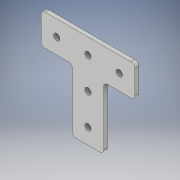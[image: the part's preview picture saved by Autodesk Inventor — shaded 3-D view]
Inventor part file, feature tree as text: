
AUTODESK INVENTOR PART (.ipt)
format: ipt  version: 2018 (Build 220112000, 112)  size: 137,728 bytes
history: native  units: in
note: dims shown in document units (in); Inventor stores cm internally (conversion verified against a paired STEP export)
features: extrude x2, sketch x2, fillet x1
ambient origin geometry x8: Origin, YZ Plane, XZ Plane, XY Plane, X Axis, Y Axis, Z Axis, Center Point
bodies: Solid1 (feature_tree)
feature tree (5):
  extrude  "Extrusion1"  Depth=3.0in
  extrude  "Extrusion2"  Depth=1.0in
  fillet  "Fillet1"  Radius=1.0in
  sketch  "Sketch1"  dims[d0=1.0in d1=3.0in]
  sketch  "Sketch2"  dims[d2=1.0in d3=1.0in d4=1.0in d5=1.0in d6=0.125in d7=0.0in d8=0.5in d9=1.0in d10=1.0in d11=1.0in d12=1.0in d13=0.2031in d14=0.125in d15=0.0in d16=0.125in]
